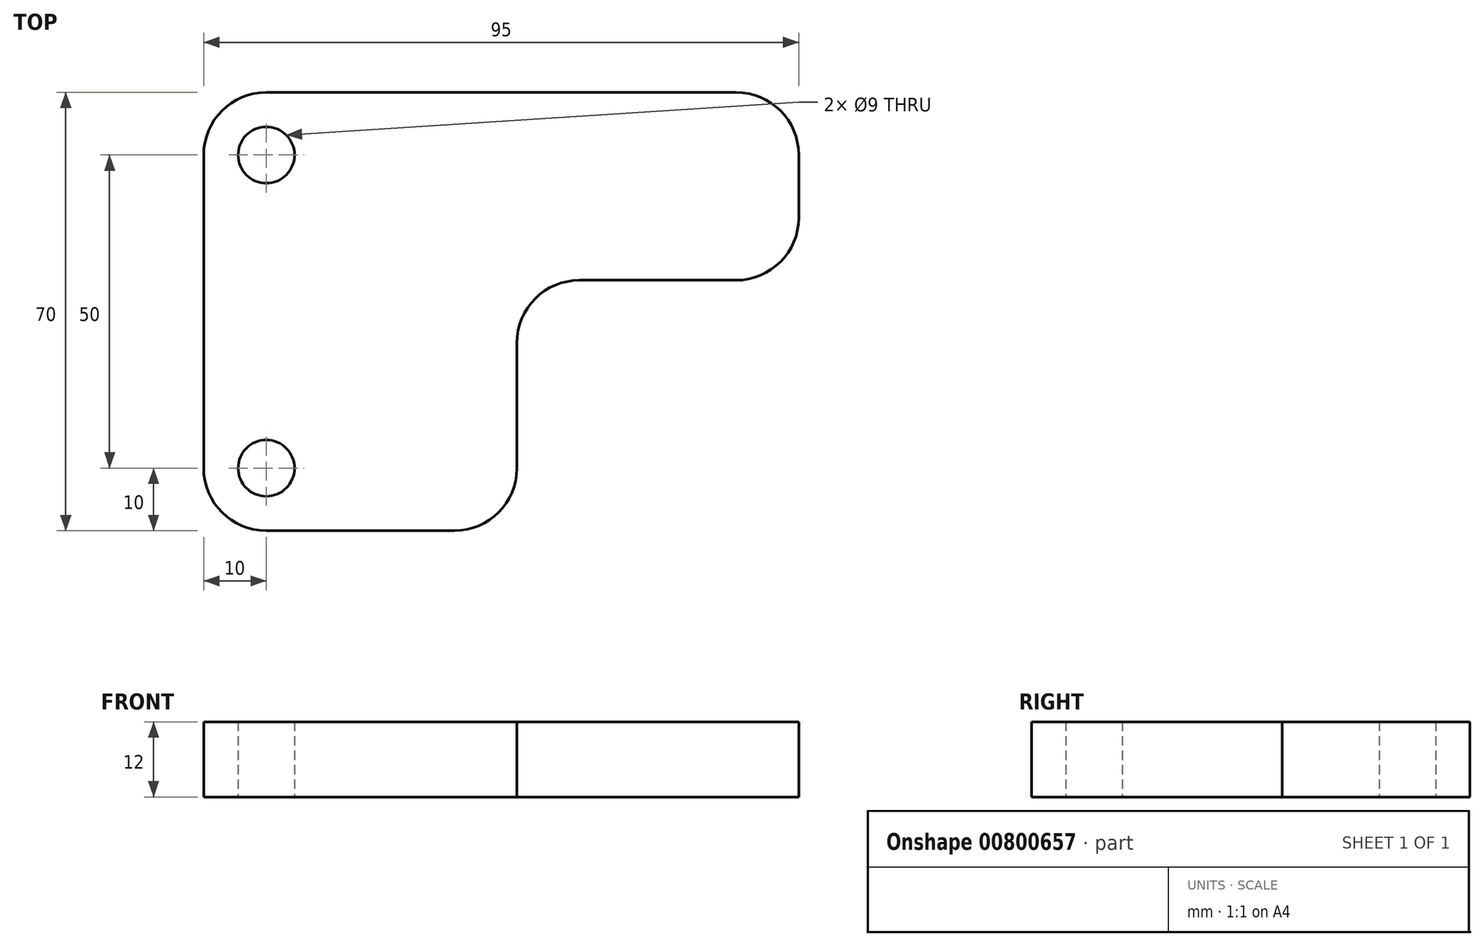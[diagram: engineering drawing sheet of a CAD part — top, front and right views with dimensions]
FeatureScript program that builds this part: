
annotation { "Feature Type Name" : "Feature", "Feature Type Description" : "" }
export const myFeature = defineFeature(function(context is Context, id is Id, definition is map)
    precondition{}
    {
        {
            var Q0;
            Q0=qCreatedBy(makeId("Top.planeOp"),FACE);
            var sketch = newSketch(context, id + "F0", { "sketchPlane" : qUnion([Q0])});
            skLineSegment(sketch, "E0", {"start": v(10, 0) * mm, "end": v(35, 0) * mm});
            skLineSegment(sketch, "E1", {"start": v(45, 10) * mm, "end": v(45, 20) * mm});
            skLineSegment(sketch, "E2", {"start": v(35, 30) * mm, "end": v(-40, 30) * mm});
            skLineSegment(sketch, "E3", {"start": v(-50, 20) * mm, "end": v(-50, -30) * mm});
            skLineSegment(sketch, "E4", {"start": v(-40, -40) * mm, "end": v(-10, -40) * mm});
            skLineSegment(sketch, "E5", {"start": v(0, -10) * mm, "end": v(0, -30) * mm});
            skPoint(sketch, "E6.visualSharp", {"position": v(45, 30) * mm});
            skArc(sketch, "E6.filletArc", {"start": v(45, 20) * mm, "mid": v(42.07, 27.07) * mm, "end": v(35, 30) * mm});
            skPoint(sketch, "E7.visualSharp", {"position": v(-50, 30) * mm});
            skArc(sketch, "E7.filletArc", {"start": v(-40, 30) * mm, "mid": v(-47.07, 27.07) * mm, "end": v(-50, 20) * mm});
            skPoint(sketch, "E8.visualSharp", {"position": v(-50, -40) * mm});
            skArc(sketch, "E8.filletArc", {"start": v(-50, -30) * mm, "mid": v(-47.07, -37.07) * mm, "end": v(-40, -40) * mm});
            skPoint(sketch, "E9.visualSharp", {"position": v(0, -40) * mm});
            skArc(sketch, "E9.filletArc", {"start": v(-10, -40) * mm, "mid": v(-2.93, -37.07) * mm, "end": v(0, -30) * mm});
            skPoint(sketch, "E10.visualSharp", {"position": v(0, 0) * mm});
            skArc(sketch, "E10.filletArc", {"start": v(10, 0) * mm, "mid": v(2.93, -2.93) * mm, "end": v(0, -10) * mm});
            skPoint(sketch, "E11.visualSharp", {"position": v(45, 0) * mm});
            skArc(sketch, "E11.filletArc", {"start": v(35, 0) * mm, "mid": v(42.07, 2.93) * mm, "end": v(45, 10) * mm});
            skCircle(sketch, "E12", {"center": v(-40, 20) * mm, "radius": 4.5 * mm});
            skCircle(sketch, "E13", {"center": v(-40, -30) * mm, "radius": 4.5 * mm});
            skSolve(sketch);
        }
        {
            var Q0;
            Q0=makeQuery(id+"F0.imprint","IMPRINT",FACE,{"disambiguationData":[TD([[makeQuery(id+"F0.imprint","IMPRINT",EDGE,{"derivedFrom":sQuery(id+"F0.wireOp",EDGE,"E0")}),1.0]])]});
            extrude(context, id + "F1", {"entities" : qUnion([Q0]), "depth" : 12 * mm, "offsetDistance" : 25 * mm});
        }
    });
